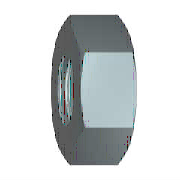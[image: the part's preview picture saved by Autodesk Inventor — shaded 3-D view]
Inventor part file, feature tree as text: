
AUTODESK INVENTOR PART (.ipt)
format: ipt  version: 2023.1 (Build 271208000, 208)  size: 171,520 bytes
history: native  units: mm (DEFAULTED — no unit token found)
features: sketch x3, chamfer x1, hole x1, other x1, plane x1
ambient origin geometry x7: Origin, YZ Plane, XZ Plane, X Axis, Y Axis, Z Axis, Center Point
bodies: Solid1 (feature_tree), Body (feature_tree)
feature tree (7):
  chamfer  "Chamfer1"  Angle=30.0deg  [1 undecoded]
  hole  "Thread"  [1 undecoded]
  other  "Work Axis1"
  plane  "Work Plane1"
  sketch  "Sketch1"  dims[d0=27.712813mm]
  sketch  "Sketch2"  dims[d1=16.4mm]
  sketch  "Sketch3"  dims[d2=0.0mm d3=30.0deg d4=30.0deg d5=24.0mm d6=24.0mm d7=90.0deg d25=13.835mm d26=6.0mm d27=4.0mm d28=2.0mm d29=14.3117mm d30=8.0mm d31=20.594885mm d8=1.082532mm d9=30.0deg d10=1.082532mm d11=30.0deg d13=0.0mm d14=0.0mm d39=0.0mm d40=1.082532mm d41=1.082532mm d42=0.0mm]
note: 2 required parameter values undecoded (feature->parameter linkage not recoverable at this tier; creation-order binding heuristic only, values carry confidence <= 0.55)
